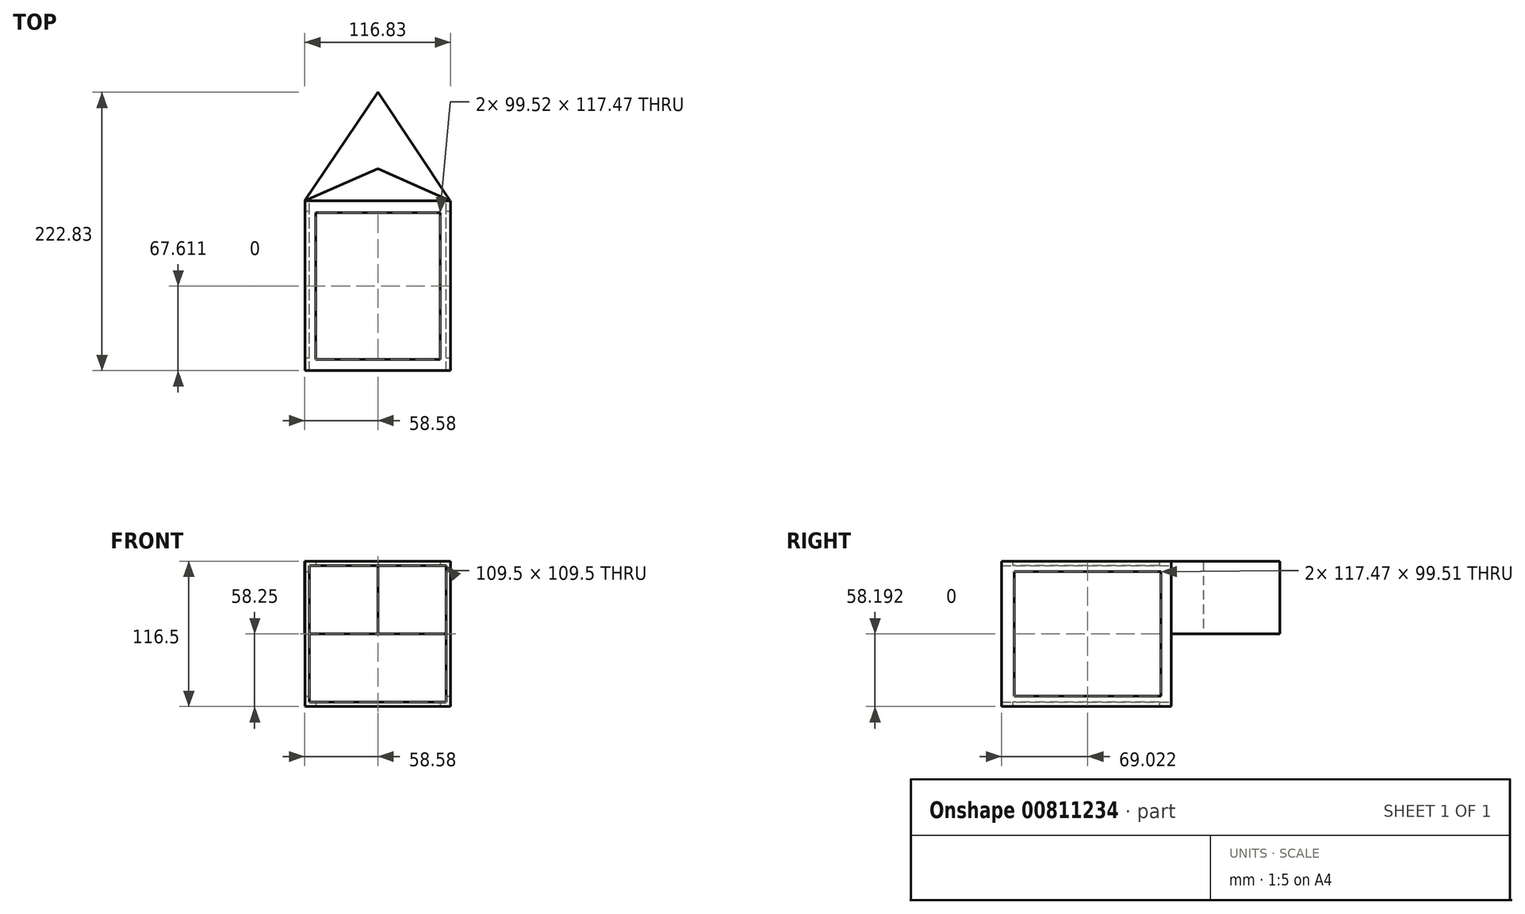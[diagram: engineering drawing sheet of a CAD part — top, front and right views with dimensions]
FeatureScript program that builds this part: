
annotation { "Feature Type Name" : "Feature", "Feature Type Description" : "" }
export const myFeature = defineFeature(function(context is Context, id is Id, definition is map)
    precondition{}
    {
        {
            var Q0;
            Q0=qCreatedBy(makeId("Front.planeOp"),FACE);
            var sketch = newSketch(context, id + "F0", { "sketchPlane" : qUnion([Q0])});
            skLineSegment(sketch, "E0.bottom", {"start": v(54.75, -54.75) * mm, "end": v(-54.75, -54.75) * mm});
            skLineSegment(sketch, "E0.top", {"start": v(54.75, 54.75) * mm, "end": v(-54.75, 54.75) * mm});
            skLineSegment(sketch, "E0.left", {"start": v(54.75, -54.75) * mm, "end": v(54.75, 54.75) * mm});
            skLineSegment(sketch, "E0.right", {"start": v(-54.75, -54.75) * mm, "end": v(-54.75, 54.75) * mm});
            skPoint(sketch, "E0.middle", {"position": v(0, 0) * mm});
            skLineSegment(sketch, "E1.bottom", {"start": v(58.25, -58.25) * mm, "end": v(-58.25, -58.25) * mm});
            skLineSegment(sketch, "E1.top", {"start": v(58.25, 58.25) * mm, "end": v(-58.25, 58.25) * mm});
            skLineSegment(sketch, "E1.left", {"start": v(58.25, -58.25) * mm, "end": v(58.25, 58.25) * mm});
            skLineSegment(sketch, "E1.right", {"start": v(-58.25, -58.25) * mm, "end": v(-58.25, 58.25) * mm});
            skSolve(sketch);
        }
        {
            var Q0;
            Q0 = qSketchRegion(id + "F0", true);
            extrude(context, id + "F1", {"entities" : qUnion([Q0]), "depth" : 136 * mm, "offsetDistance" : 25 * mm});
        }
        {
            var Q0;
            Q0=makeQuery(id+"F1.opExtrude","SWEPT_FACE",FACE,{"disambiguationData":[OSD([sQuery(id+"F0.wireOp",EDGE,"E1.bottom")])]});
            var sketch = newSketch(context, id + "F2", { "sketchPlane" : qUnion([Q0])});
            skLineSegment(sketch, "E2.bottom", {"start": v(49.76, 9.65) * mm, "end": v(-49.76, 9.65) * mm});
            skLineSegment(sketch, "E2.top", {"start": v(49.76, 127.12) * mm, "end": v(-49.76, 127.12) * mm});
            skLineSegment(sketch, "E2.left", {"start": v(49.76, 9.65) * mm, "end": v(49.76, 127.12) * mm});
            skLineSegment(sketch, "E2.right", {"start": v(-49.76, 9.65) * mm, "end": v(-49.76, 127.12) * mm});
            skPoint(sketch, "E2.middle", {"position": v(0, 68.39) * mm});
            skSolve(sketch);
        }
        {
            var Q0;
            Q0 = qSketchRegion(id + "F2", true);
            extrude(context, id + "F3", {"entities" : qUnion([Q0]), "operationType" : NewBodyOperationType.REMOVE, "oppositeDirection" : true, "depth" : 186 * mm, "offsetDistance" : 25 * mm});
        }
        {
            var Q0;
            Q0=makeQuery(id+"F1.opExtrude","SWEPT_FACE",FACE,{"disambiguationData":[OSD([sQuery(id+"F0.wireOp",EDGE,"E1.left")])]});
            var sketch = newSketch(context, id + "F4", { "sketchPlane" : qUnion([Q0])});
            skLineSegment(sketch, "E3.bottom", {"start": v(-8.24, 49.7) * mm, "end": v(-8.24, -49.82) * mm});
            skLineSegment(sketch, "E3.top", {"start": v(-125.71, 49.7) * mm, "end": v(-125.71, -49.82) * mm});
            skLineSegment(sketch, "E3.left", {"start": v(-8.24, 49.7) * mm, "end": v(-125.71, 49.7) * mm});
            skLineSegment(sketch, "E3.right", {"start": v(-8.24, -49.82) * mm, "end": v(-125.71, -49.82) * mm});
            skSolve(sketch);
        }
        {
            var Q0;
            Q0=makeQuery(id+"F4.imprint","IMPRINT",FACE,{"disambiguationData":[TD([[makeQuery(id+"F4.imprint","IMPRINT",EDGE,{"derivedFrom":sQuery(id+"F4.wireOp",EDGE,"E3.bottom")}),-1.0]])]});
            extrude(context, id + "F5", {"entities" : qUnion([Q0]), "operationType" : NewBodyOperationType.REMOVE, "oppositeDirection" : true, "depth" : 134.2 * mm, "offsetDistance" : 25 * mm});
        }
        {
            var Q0;
            Q0=qCreatedBy(makeId("Top.planeOp"),FACE);
            var sketch = newSketch(context, id + "F6", { "sketchPlane" : qUnion([Q0])});
            skLineSegment(sketch, "E4", {"start": v(-58.58, 0) * mm, "end": v(0, 86.83) * mm});
            skLineSegment(sketch, "E5", {"start": v(0, 86.83) * mm, "end": v(57.7, 0) * mm});
            skLineSegment(sketch, "E6", {"start": v(-58.58, 0) * mm, "end": v(0, 25.7) * mm});
            skLineSegment(sketch, "E7", {"start": v(0, 25.7) * mm, "end": v(57.7, 0) * mm});
            skSolve(sketch);
        }
        {
            var Q0;
            Q0=makeQuery(id+"F6.imprint","IMPRINT",FACE,{"disambiguationData":[TD([[makeQuery(id+"F6.imprint","IMPRINT",EDGE,{"derivedFrom":sQuery(id+"F6.wireOp",EDGE,"E4")}),-1.0]])]});
            extrude(context, id + "F7", {"entities" : qUnion([Q0]), "operationType" : NewBodyOperationType.ADD, "depth" : 58 * mm, "offsetDistance" : 25 * mm});
        }
    });
